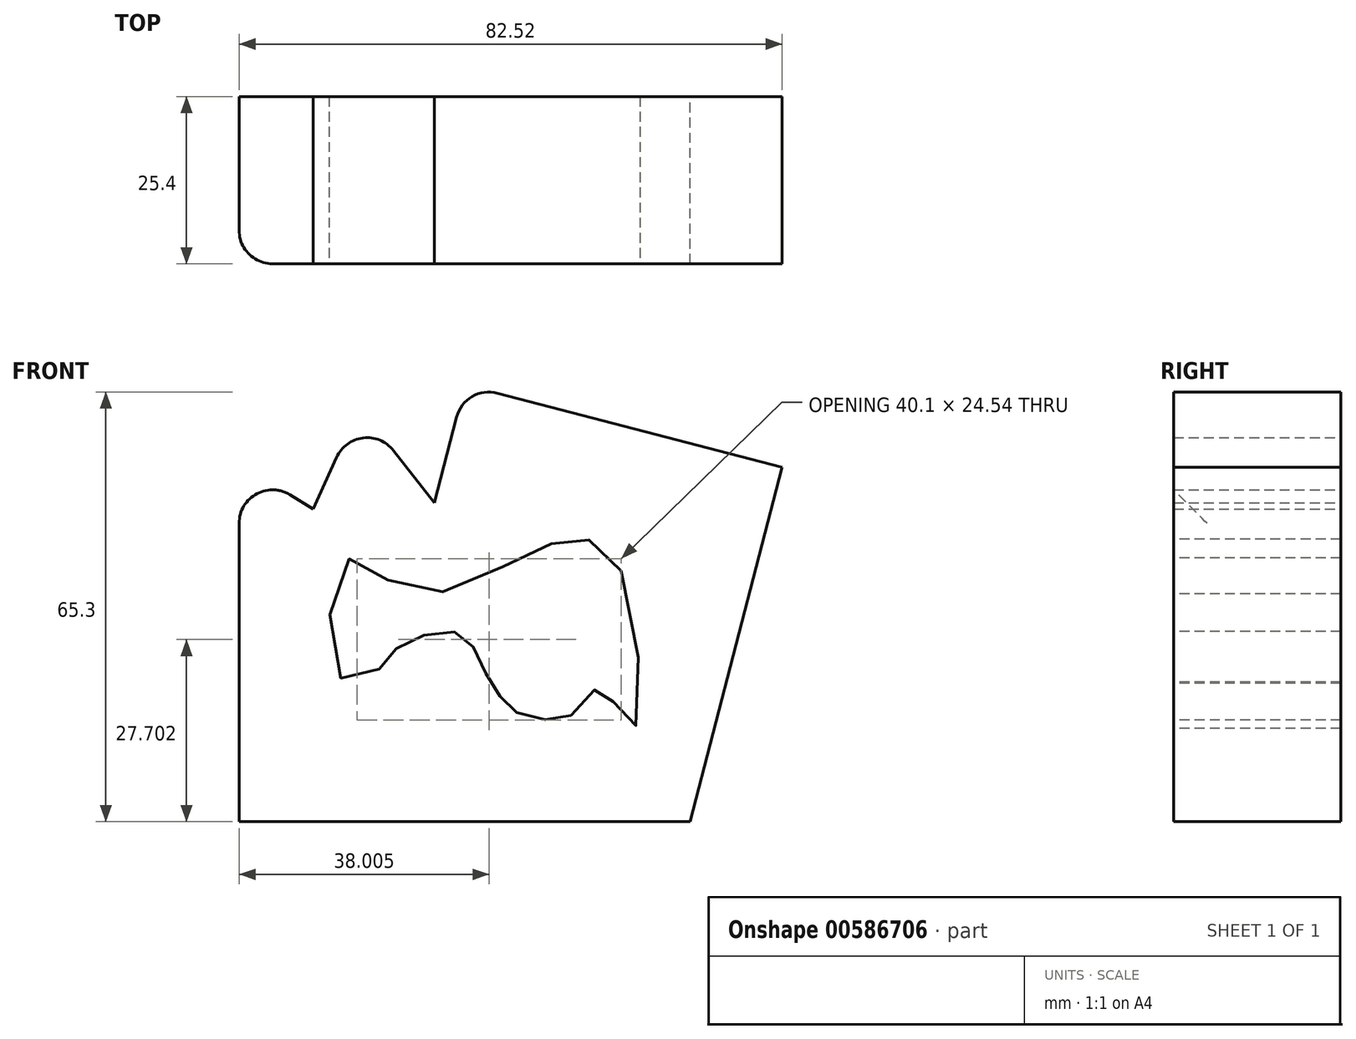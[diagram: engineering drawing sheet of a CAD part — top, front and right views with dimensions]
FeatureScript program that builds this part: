
annotation { "Feature Type Name" : "Feature", "Feature Type Description" : "" }
export const myFeature = defineFeature(function(context is Context, id is Id, definition is map)
    precondition{}
    {
        {
            var Q0;
            Q0=qCreatedBy(makeId("Front.planeOp"),FACE);
            var sketch = newSketch(context, id + "F0", { "sketchPlane" : qUnion([Q0])});
            skLineSegment(sketch, "E0", {"start": v(-44.61, 36.09) * mm, "end": v(-44.61, -18.42) * mm});
            skLineSegment(sketch, "E1", {"start": v(-44.61, -18.42) * mm, "end": v(23.9, -18.42) * mm});
            skLineSegment(sketch, "E2", {"start": v(23.9, -18.42) * mm, "end": v(37.91, 35.48) * mm});
            skLineSegment(sketch, "E3", {"start": v(37.91, 35.48) * mm, "end": v(-10.27, 48) * mm});
            skLineSegment(sketch, "E4", {"start": v(-10.27, 48) * mm, "end": v(-14.94, 30.05) * mm});
            skLineSegment(sketch, "E5", {"start": v(-14.94, 30.05) * mm, "end": v(-26.34, 44.61) * mm});
            skLineSegment(sketch, "E6", {"start": v(-26.34, 44.61) * mm, "end": v(-33.34, 29.08) * mm});
            skLineSegment(sketch, "E7", {"start": v(-33.34, 29.08) * mm, "end": v(-44.61, 36.09) * mm});
            skSolve(sketch);
        }
        {
            var Q0;
            Q0 = qSketchRegion(id + "F0", true);
            extrude(context, id + "F1", {"entities" : qUnion([Q0]), "depth" : 25.4 * mm, "offsetDistance" : 25.4 * mm});
        }
        {
            var Q0;
            Q0=makeQuery(id+"F1.opExtrude","SWEPT_EDGE",EDGE,{"disambiguationData":[OSD([sQuery(id+"F0.wireOp",EDGE,"E5"),sQuery(id+"F0.wireOp",EDGE,"E6")])]});
            var Q1;
            Q1=makeQuery(id+"F1.opExtrude","SWEPT_EDGE",EDGE,{"disambiguationData":[OSD([sQuery(id+"F0.wireOp",EDGE,"E3"),sQuery(id+"F0.wireOp",EDGE,"E4")])]});
            var Q2;
            Q2=makeQuery(id+"F1.opExtrude","SWEPT_EDGE",EDGE,{"disambiguationData":[OSD([sQuery(id+"F0.wireOp",EDGE,"E0"),sQuery(id+"F0.wireOp",EDGE,"E7")])]});
            var Q3;
            Q3=makeQuery(id+"F1.opExtrude","CAP_EDGE",EDGE,{"disambiguationData":[OSD([sQuery(id+"F0.wireOp",EDGE,"E0")])],"isStart":false});
            fillet(context, id + "F2", {"entities" : qUnion([Q0, Q1, Q2, Q3]), "radius" : 5.08 * mm, "tangentPropagation" : true, "allowEdgeOverflow" : false});
        }
        {
            var Q0;
            Q0=makeQuery(id+"F1.opExtrude","CAP_FACE",FACE,{"disambiguationData":[OSD([sQuery(id+"F0.wireOp",EDGE,"E0"),sQuery(id+"F0.wireOp",EDGE,"E1"),sQuery(id+"F0.wireOp",EDGE,"E2"),sQuery(id+"F0.wireOp",EDGE,"E3"),sQuery(id+"F0.wireOp",EDGE,"E4"),sQuery(id+"F0.wireOp",EDGE,"E5"),sQuery(id+"F0.wireOp",EDGE,"E6"),sQuery(id+"F0.wireOp",EDGE,"E7")])],"isStart":false});
            var sketch = newSketch(context, id + "F3", { "sketchPlane" : qUnion([Q0])});
            skFitSpline(sketch, "E8", {"points": [v(13.45, 19.7) * mm, v(6.92, 24.56) * mm, v(-1.92, 21.74) * mm, v(-18.95, 16.62) * mm, v(-28.17, 21.36) * mm, v(-29.19, 3.44) * mm, v(-22.4, 5.61) * mm, v(-20.87, 7.79) * mm, v(-17.15, 9.7) * mm, v(-12.29, 10.48) * mm, v(-9.98, 9.45) * mm, v(-7.94, 6) * mm, v(-6.4, 2.8) * mm, v(-4.48, 0) * mm, v(-2.69, -1.69) * mm, v(1.41, -2.84) * mm, v(4.1, -2.84) * mm, v(8.58, 0) * mm, v(10.37, 2.54) * mm, v(15.11, -4.25) * mm, v(13.45, 19.7) * mm]});
            skSolve(sketch);
        }
        {
            var Q0;
            Q0=makeQuery(id+"F3.imprint","IMPRINT",FACE,{"disambiguationData":[TD([[makeQuery(id+"F3.imprint","IMPRINT",EDGE,{"derivedFrom":sQuery(id+"F3.wireOp",EDGE,"E8")}),1.0]])]});
            extrude(context, id + "F4", {"entities" : qUnion([Q0]), "operationType" : NewBodyOperationType.REMOVE, "oppositeDirection" : true, "depth" : 25.4 * mm, "offsetDistance" : 25.4 * mm});
        }
    });
